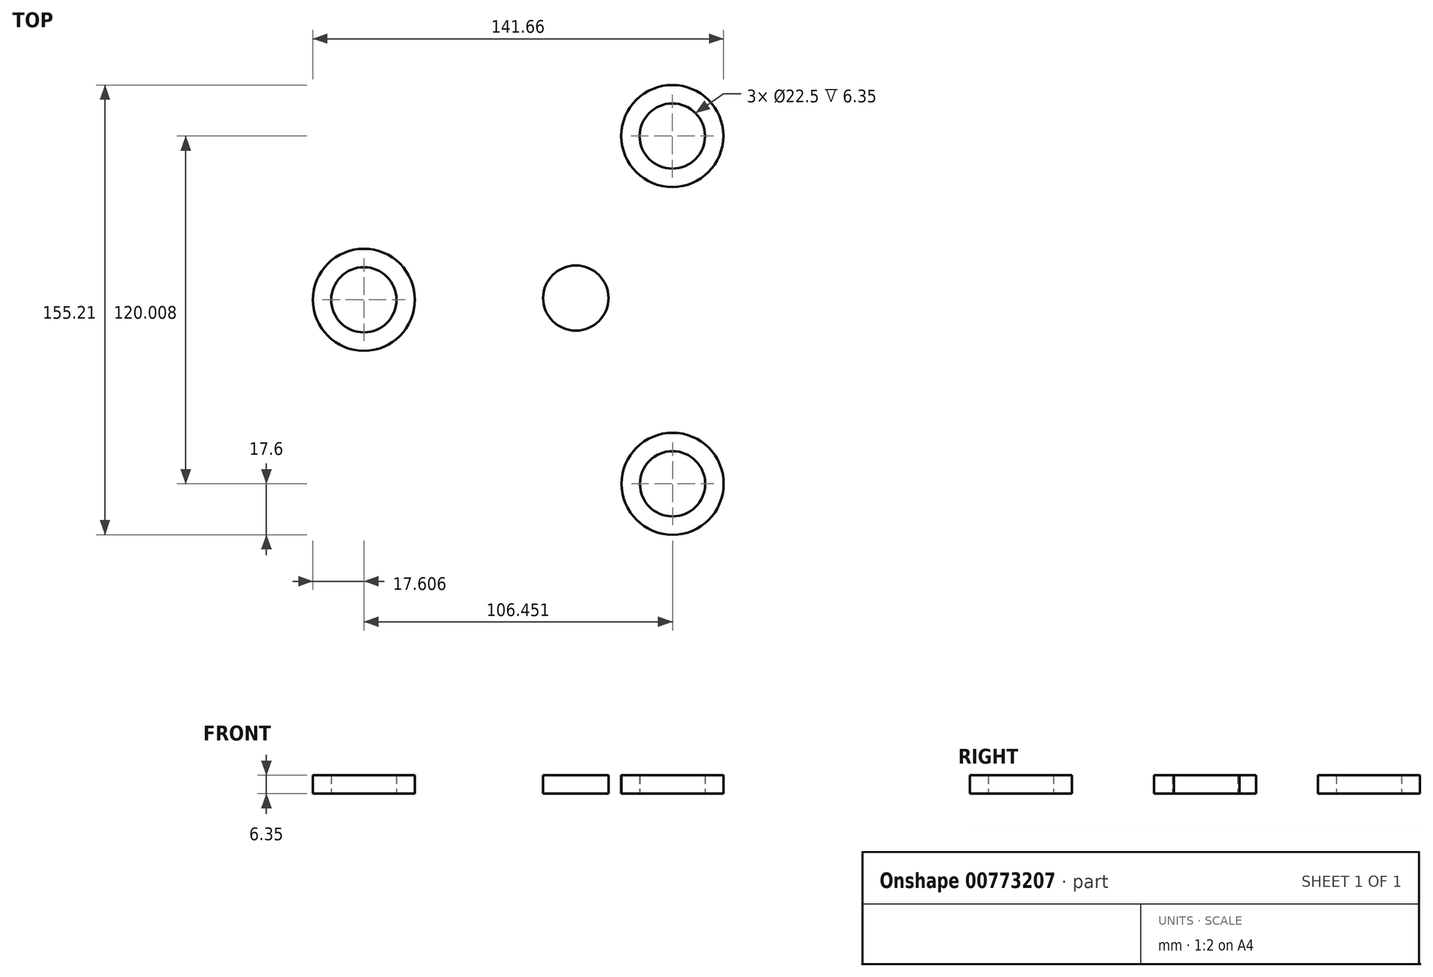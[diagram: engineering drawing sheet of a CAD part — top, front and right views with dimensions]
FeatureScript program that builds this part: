
annotation { "Feature Type Name" : "Feature", "Feature Type Description" : "" }
export const myFeature = defineFeature(function(context is Context, id is Id, definition is map)
    precondition{}
    {
        {
            var Q0;
            Q0=qCreatedBy(makeId("Top.planeOp"),FACE);
            var sketch = newSketch(context, id + "F0", { "sketchPlane" : qUnion([Q0])});
            skCircle(sketch, "E0", {"center": v(-22.5, 0) * mm, "radius": 11.25 * mm});
            skCircle(sketch, "E1", {"center": v(50.57, 0.59) * mm, "radius": 11.25 * mm});
            skCircle(sketch, "E2.0", {"center": v(-22.5, 0) * mm, "radius": 17.6 * mm});
            skCircle(sketch, "E3.1.0", {"center": v(83.95, -63.5) * mm, "radius": 11.25 * mm});
            skCircle(sketch, "E3.2.0", {"center": v(83.86, 56.5) * mm, "radius": 11.25 * mm});
            skCircle(sketch, "E4.0", {"center": v(83.86, 56.5) * mm, "radius": 17.6 * mm});
            skCircle(sketch, "E5.0", {"center": v(83.95, -63.5) * mm, "radius": 17.6 * mm});
            skArc(sketch, "E6", {"start": v(66.34, -63.5) * mm, "mid": v(27.78, -29.21) * mm, "end": v(-22.5, -17.6) * mm});
            skSolve(sketch);
        }
        {
            var Q0;
            Q0 = qSketchRegion(id + "F0", true);
            extrude(context, id + "F1", {"entities" : qUnion([Q0]), "depth" : 6.35 * mm, "offsetDistance" : 25.4 * mm});
        }
    });
